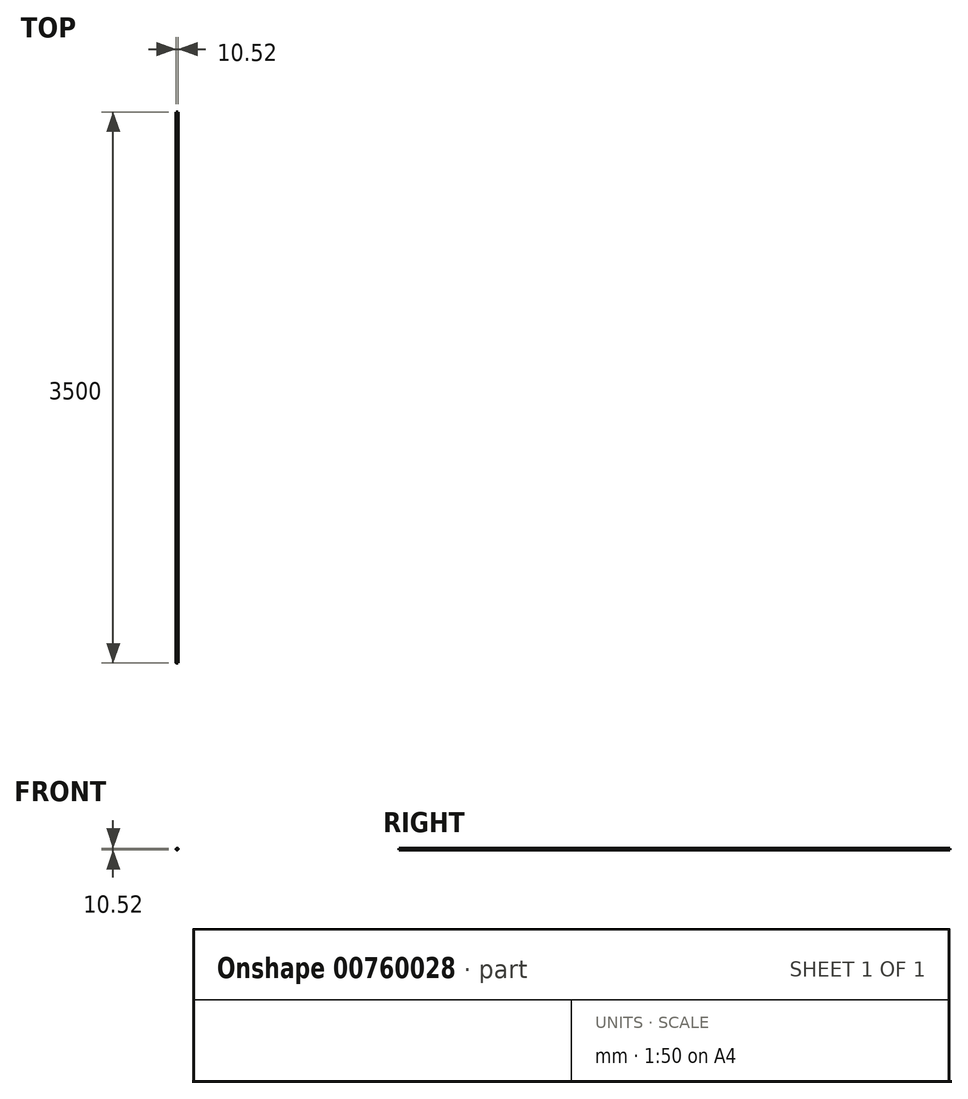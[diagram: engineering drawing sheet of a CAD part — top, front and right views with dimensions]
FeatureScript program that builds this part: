
annotation { "Feature Type Name" : "Feature", "Feature Type Description" : "" }
export const myFeature = defineFeature(function(context is Context, id is Id, definition is map)
    precondition{}
    {
        {
            var Q0;
            Q0=qCreatedBy(makeId("Front.planeOp"),FACE);
            var sketch = newSketch(context, id + "F0", { "sketchPlane" : qUnion([Q0])});
            skCircle(sketch, "E0", {"center": v(0, 0) * mm, "radius": 5.26 * mm});
            skSolve(sketch);
        }
        {
            var Q0;
            Q0=makeQuery(id+"F0.imprint","IMPRINT",FACE,{"disambiguationData":[TD([[makeQuery(id+"F0.imprint","IMPRINT",EDGE,{"derivedFrom":sQuery(id+"F0.wireOp",EDGE,"E0")}),1.0]])]});
            extrude(context, id + "F1", {"entities" : qUnion([Q0]), "oppositeDirection" : true, "depth" : 3500 * mm, "offsetDistance" : 25 * mm});
        }
    });
